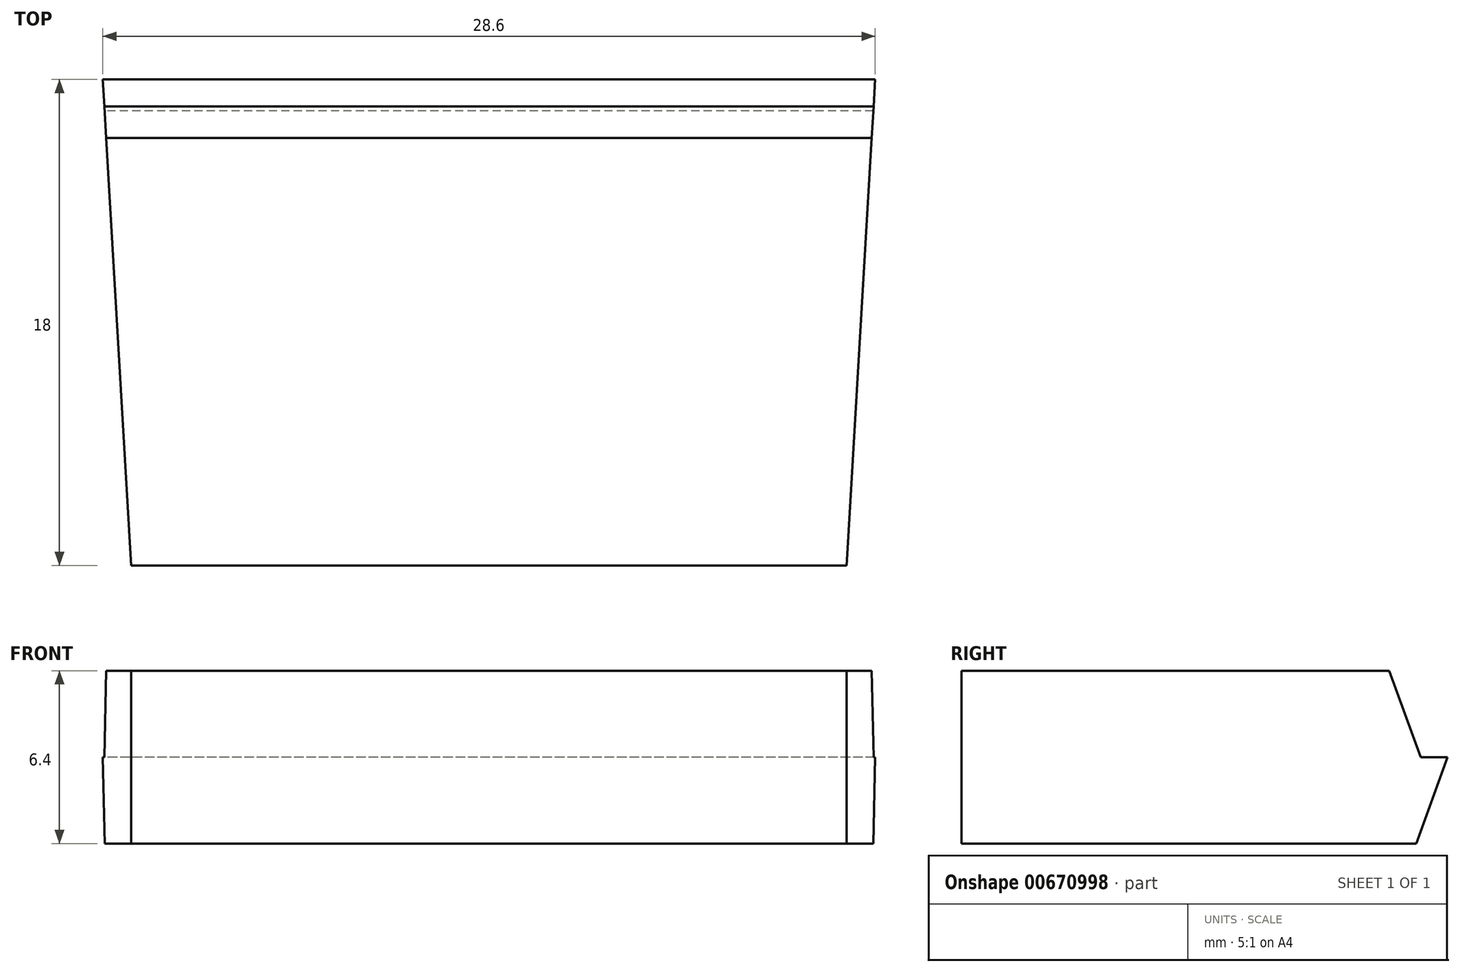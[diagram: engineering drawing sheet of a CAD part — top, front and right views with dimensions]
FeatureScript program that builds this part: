
annotation { "Feature Type Name" : "Feature", "Feature Type Description" : "" }
export const myFeature = defineFeature(function(context is Context, id is Id, definition is map)
    precondition{}
    {
        {
            var Q0;
            Q0=qCreatedBy(makeId("Right.planeOp"),FACE);
            var sketch = newSketch(context, id + "F0", { "sketchPlane" : qUnion([Q0])});
            skLineSegment(sketch, "E0", {"start": v(-18, 3.2) * mm, "end": v(-2.16, 3.2) * mm});
            skLineSegment(sketch, "E1", {"start": v(-2.16, 3.2) * mm, "end": v(-1, 0) * mm});
            skLineSegment(sketch, "E2", {"start": v(-1, 0) * mm, "end": v(0, 0) * mm});
            skLineSegment(sketch, "E3", {"start": v(0, 0) * mm, "end": v(-1.16, -3.2) * mm});
            skLineSegment(sketch, "E4", {"start": v(-1.16, -3.2) * mm, "end": v(-18, -3.2) * mm});
            skLineSegment(sketch, "E5", {"start": v(-18, -3.2) * mm, "end": v(-18, 3.2) * mm});
            skPoint(sketch, "E6", {"position": v(-18, 0) * mm});
            skSolve(sketch);
        }
        {
            var Q0;
            Q0 = qSketchRegion(id + "F0", true);
            extrude(context, id + "F1", {"entities" : qUnion([Q0]), "depth" : (28.6 / 2) * mm, "offsetDistance" : 25 * mm, "hasSecondDirection" : true, "secondDirectionOppositeDirection" : true, "secondDirectionDepth" : 14.3 * mm});
        }
        {
            var Q0;
            Q0=qCreatedBy(makeId("Top.planeOp"),FACE);
            var sketch = newSketch(context, id + "F2", { "sketchPlane" : qUnion([Q0])});
            skLineSegment(sketch, "E7", {"start": v(-14.3, 0) * mm, "end": v(-13.25, -18) * mm});
            skLineSegment(sketch, "E8", {"start": v(-13.25, -18) * mm, "end": v(13.25, -18) * mm});
            skLineSegment(sketch, "E9", {"start": v(13.25, -18) * mm, "end": v(14.3, 0) * mm});
            skLineSegment(sketch, "E10", {"start": v(14.3, 0) * mm, "end": v(17.08, 0) * mm});
            skLineSegment(sketch, "E11", {"start": v(17.08, 0) * mm, "end": v(17.08, -21.79) * mm});
            skLineSegment(sketch, "E12", {"start": v(17.08, -21.79) * mm, "end": v(-17.08, -21.79) * mm});
            skLineSegment(sketch, "E13", {"start": v(-17.08, -21.79) * mm, "end": v(-17.08, 0) * mm});
            skLineSegment(sketch, "E14", {"start": v(-17.08, 0) * mm, "end": v(-14.3, 0) * mm});
            skSolve(sketch);
        }
        {
            var Q0;
            Q0 = qSketchRegion(id + "F2", true);
            extrude(context, id + "F3", {"entities" : qUnion([Q0]), "operationType" : NewBodyOperationType.REMOVE, "depth" : 25 * mm, "offsetDistance" : 25 * mm, "hasSecondDirection" : true, "secondDirectionOppositeDirection" : true, "secondDirectionDepth" : 25 * mm});
        }
    });
